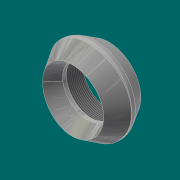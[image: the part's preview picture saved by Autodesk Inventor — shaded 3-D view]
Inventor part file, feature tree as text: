
AUTODESK INVENTOR PART (.ipt)
format: ipt  version: 2017.3 (Build 213257000, 257)  size: 370,176 bytes
history: native  units: mm (DEFAULTED — no unit token found)
features: other x8, sketch x5, plane x1, extrude x1, revolve x1, thread x1, sweep x1
ambient origin geometry x8: Origin, YZ Plane, XZ Plane, XY Plane, X Axis, Y Axis, Z Axis, Center Point
bodies: Solid1 (feature_tree)
feature tree (18):
  sketch  "Sketch1"  dims[d5=38.1mm d8=90.0deg]
  plane  "Work Plane1"
  sketch  "Sketch2"  dims[d9=0.0mm d10=866.775mm d11=10.0mm d12=0.0mm]
  extrude  "Extrusion1"  TaperAngle=90.0deg  [1 undecoded]
  revolve  "Revolution2"  [1 undecoded]
  thread  "Thread1"  [1 undecoded]
  other  "Work Point1"
  sweep  "Sweep1"
  other  "Work Axis3"
  other  "Work Point2"
  other  "Work Point3"
  sketch  "Sketch3"  dims[d45=8.810625mm d52=88.10625mm]
  sketch  "Sketch4"  dims[d54=1121.56875mm d77=68.1482mm d80=38.1mm d81=19.2151mm d83=56.55818mm d85=0.312398mm d86=90.0deg d91=52.5018mm d92=6.0mm d93=4.0mm d94=2.0mm d95=90.0deg d96=3.84302mm d97=0.0mm d102=10.0mm d103=0.0mm d106=19.05mm d107=471.4875mm d120=-433.3875mm d121=0.0mm d129=0.78232mm d130=0.78232mm d131=30.0deg d132=11.509375mm d133=0.0mm d134=0.0mm d135=90.0deg d136=0.0mm d137=90.0deg d138=65.0875mm d139=58.3692mm d140=0.0mm]
  other  "Work Axis2"
  sketch  "3D Sketch1"
  other  "Edges14"
  other  "Edges15"
  other  "Work Axis4"
note: 3 required parameter values undecoded (feature->parameter linkage not recoverable at this tier; creation-order binding heuristic only, values carry confidence <= 0.55)